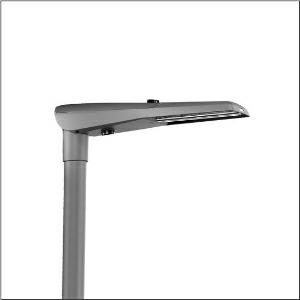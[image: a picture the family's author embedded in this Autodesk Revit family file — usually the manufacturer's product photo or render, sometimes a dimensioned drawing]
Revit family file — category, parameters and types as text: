
# Revit family: streetlight_sl_11_iq_mini___st1_2a_5xc2ac1y08ge_2c74
name_source: partatom
category: Lighting Fixtures
units: mm (PartAtom-declared; Revit-internal decimal feet)

## family parameters
Cut with Voids When Loaded = No
Host = Face
Light Source = No
Part Type = Normal
Room Calculation Point = No
Round Connector Dimension = Use Diameter
Shared = No

## types (1)
- --- (1 x LED, 3040 lm, 25.3 W, 2200K)
    Apparent Load = 25 VA
    CIE Flux Codes = 32 70 96 100 100
    Color Rendering = 70
    Color Temperature = 2200K
    Default Elevation = 1800 mm
    Description = Streetlight SL 11 iQ mini, mast luminaire, primary light control with 3 zone facetted reflector, of plastic, silver coated, highly specular, primary optical cover: cover, of PMMA, transparent, light distribution: ST1.2a, light emission: direct distribution, primary light characteristic: asymmetric, installation type: post-top, side-entry, lamps: LED, High Power LED, rated values: 3.570lm | 24,9W | 143,4lm/W (begin service life); end service life: 3.570lm | 25,7W; at 50% lumin. flux: 1.785lm | 12,8W | 139,5lm/W, colour temperature: 2200/2700/3000/4000K, colour rendering: CRI > 70, light colour: 722/727/730/740, light setting 1 begin service life: 100% | 3.570lm | 24,9W | 143,4lm/W | 3.000K, light setting 1 end service life: 25,7W, further light settings possible, control: pre-setting: logarithmic dimming characteristic, Street-Remote, Auto-Match, Temp-Guard, Lumen-Switch, Night-Set, Smart-Wire, Light-Fading, Desk-Remote (wireless, voltage-free reading and setting of iQ features in the workshop via application-optimized NFC function/RFID function), optimised constant luminous flux control (CLO 2.0), with cable H07RN-F 5x 1.5mm², mains connection: 230..240V, AC, 50/60Hz, connection cable pre-assembled, cable length: 6,5m, luminaire housing, of diecast aluminium, powder-coated, Siteco® metallic grey (DB 702S), please order mast flange separately, inclination adjustable without tools: 0°, 5°, 10°, 15° (post-top) | 0°, -5°, -10°, -15° (side-entry), sealing non-destructively replaceable, multi-level sealing system, length: 736mm, width: 174mm, height: 116mm, mast flange for spigot size: 42mm (side-entry): 5XC10008XM4, 60/48mm (side-entry/post-top): 5XC10108XM2, 76/60mm (side-entry/post-top): 5XC10108XM1, equipment: standard, Smart Interface below and above, protection rating (complete): IP66, insulation class (complete): insulation class II (safety insulation), certification: CE, ENEC, ENEC+, VDE, UKCA, impact resistance: IK10, permissible operating ambient temperature for outdoor applications: -25..+50°C, standard-compliant lighting for roads and squares, Environmental Product Declaration (EPD) tested and certified by an independent institute, packaging unit: 1 piece

Light Distribution: ST1.2a
    Height = 116 mm
    Lamp = 1 x LED
    Lamp Light Flux = 3040 lm
    Lamp Power = 25.3 W
    Lamp count = 1
    Length = 736 mm
    Luminous efficacy = 120 lm/W
    Manufacturer = Siteco
    ModVariant = No
    Model = 5XC2AC1Y08GE
    Number of Poles = 1
    OnlyDefault = Yes
    Power Factor = 1
    Product Name = Streetlight SL 11 iQ mini | ST1.2a
    Product group = mast luminaire | pylon top
    ProductGroupID = 6100
    Protection Class = Protection class II
    Protection Degree = IP 66
    RLX_Detail_Level = 1
    RLX_Emergency_Light_Flux = 0 lm
    RLX_Emergency_Type = 0
    RLX_Emergency_Type_DB = No
    RlxData = <blob elided: 53669 chars, md5=bb17d78a>
    Socket = socket
    Standby Power = 0 W
    System Light Flux = 3040 lm
    System Power = 25 W
    Type Comments = individual setting: luminous flux: 100 % | dim-lin: 254 | 351 mA
    Type Image = l_1006751.jpg
    URL = http://relux.com
    VarID = @adj_055477
    Voltage = 0 V
    Weight = 0.00 kg
    Width = 174 mm

## geometry (parser evidence)
native form markers: Blend x4, Sweep x10
no freeform markers — native parametric forms only
